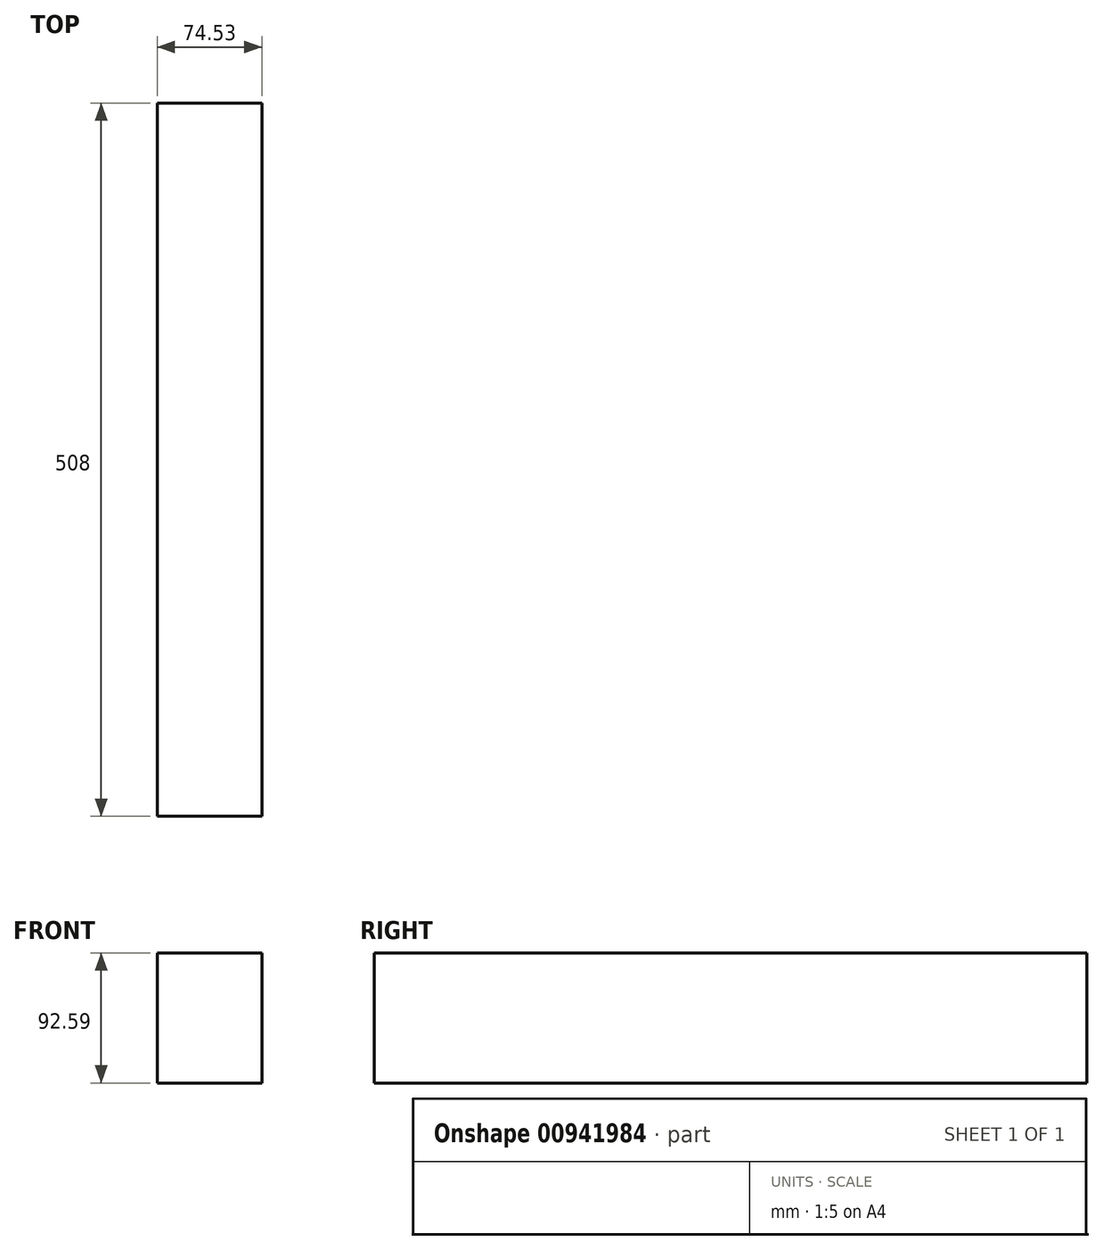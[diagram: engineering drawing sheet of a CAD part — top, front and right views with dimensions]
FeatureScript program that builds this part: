
annotation { "Feature Type Name" : "Feature", "Feature Type Description" : "" }
export const myFeature = defineFeature(function(context is Context, id is Id, definition is map)
    precondition{}
    {
        {
            var Q0;
            Q0=qCreatedBy(makeId("Front.planeOp"),FACE);
            var sketch = newSketch(context, id + "F0", { "sketchPlane" : qUnion([Q0])});
            skLineSegment(sketch, "E0.bottom", {"start": v(0, -63.15) * mm, "end": v(74.53, -63.15) * mm});
            skLineSegment(sketch, "E0.top", {"start": v(0, 29.44) * mm, "end": v(74.53, 29.44) * mm});
            skLineSegment(sketch, "E0.left", {"start": v(0, -63.15) * mm, "end": v(0, 29.44) * mm});
            skLineSegment(sketch, "E0.right", {"start": v(74.53, -63.15) * mm, "end": v(74.53, 29.44) * mm});
            skSolve(sketch);
        }
        {
            var Q0;
            Q0 = qSketchRegion(id + "F0", true);
            extrude(context, id + "F1", {"entities" : qUnion([Q0]), "depth" : 508 * mm, "offsetDistance" : 25.4 * mm});
        }
    });
